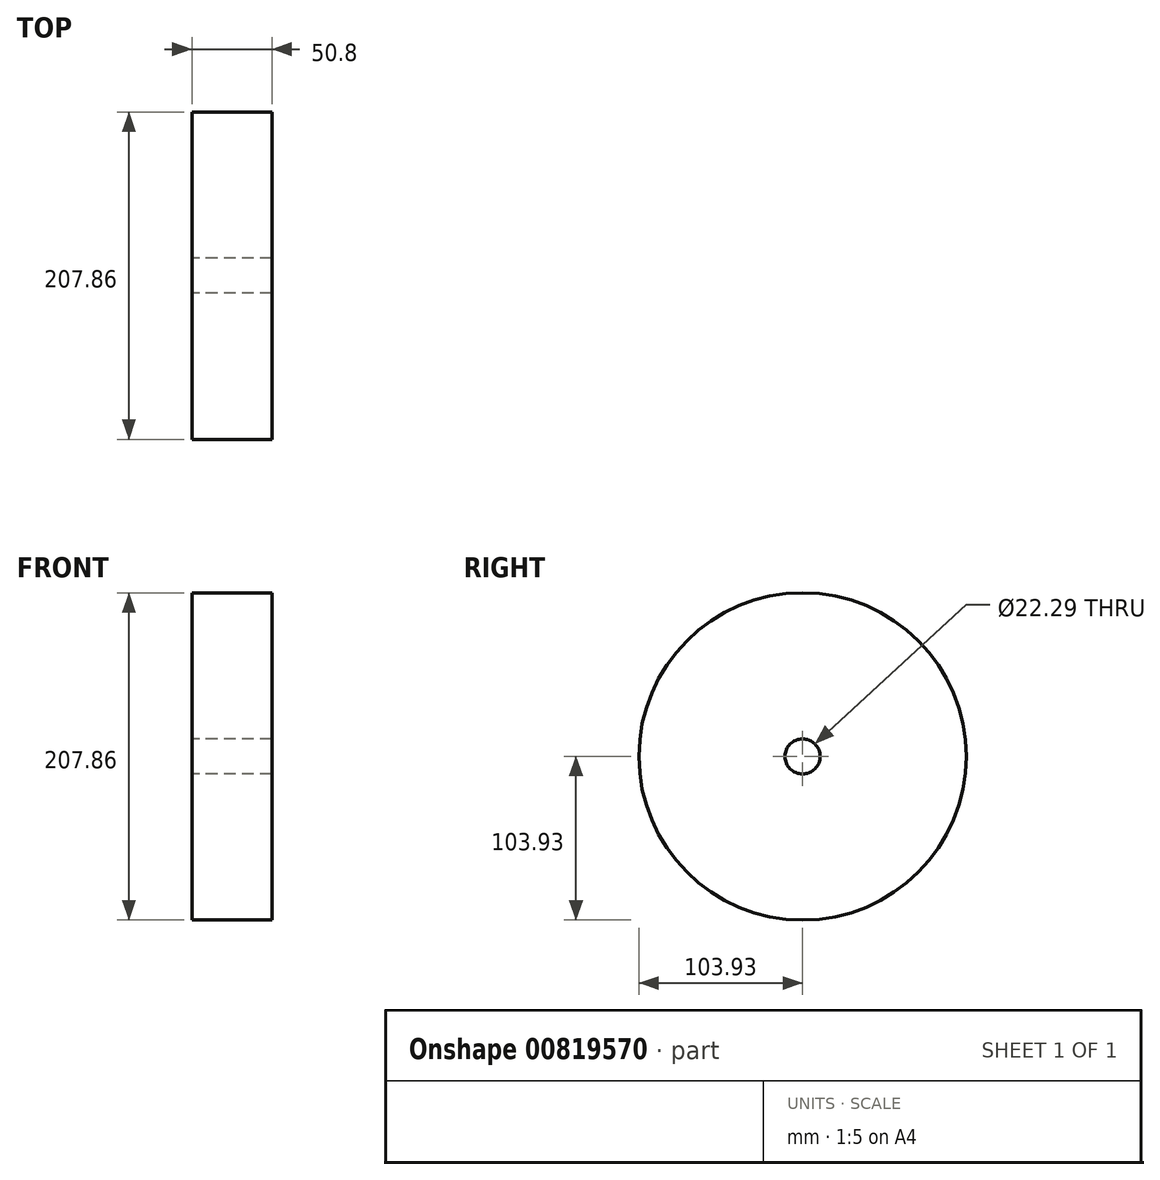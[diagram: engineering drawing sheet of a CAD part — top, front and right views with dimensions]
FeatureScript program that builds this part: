
annotation { "Feature Type Name" : "Feature", "Feature Type Description" : "" }
export const myFeature = defineFeature(function(context is Context, id is Id, definition is map)
    precondition{}
    {
        {
            var Q0;
            Q0=qCreatedBy(makeId("Right.planeOp"),FACE);
            var sketch = newSketch(context, id + "F0", { "sketchPlane" : qUnion([Q0])});
            skCircle(sketch, "E0", {"center": v(0, 0) * mm, "radius": 103.93 * mm});
            skCircle(sketch, "E1", {"center": v(0, 0) * mm, "radius": 11.15 * mm});
            skSolve(sketch);
        }
        {
            var Q0;
            Q0=makeQuery(id+"F0.imprint","IMPRINT",FACE,{"disambiguationData":[TD([[makeQuery(id+"F0.imprint","IMPRINT",EDGE,{"derivedFrom":sQuery(id+"F0.wireOp",EDGE,"E0")}),1.0]])]});
            extrude(context, id + "F1", {"entities" : qUnion([Q0]), "depth" : 25.4 * mm, "offsetDistance" : 25.4 * mm, "hasSecondDirection" : true, "secondDirectionOppositeDirection" : true, "secondDirectionDepth" : 25.4 * mm});
        }
        {
            var Q0;
            Q0=sQuery(id+"F0.wireOp",EDGE,"E1");
            extrude(context, id + "F2", {"bodyType" : ToolBodyType.SURFACE, "surfaceEntities" : qUnion([Q0]), "depth" : 25.4 * mm, "offsetDistance" : 25.4 * mm, "hasSecondDirection" : true, "secondDirectionOppositeDirection" : true, "secondDirectionDepth" : 25.4 * mm});
        }
    });
